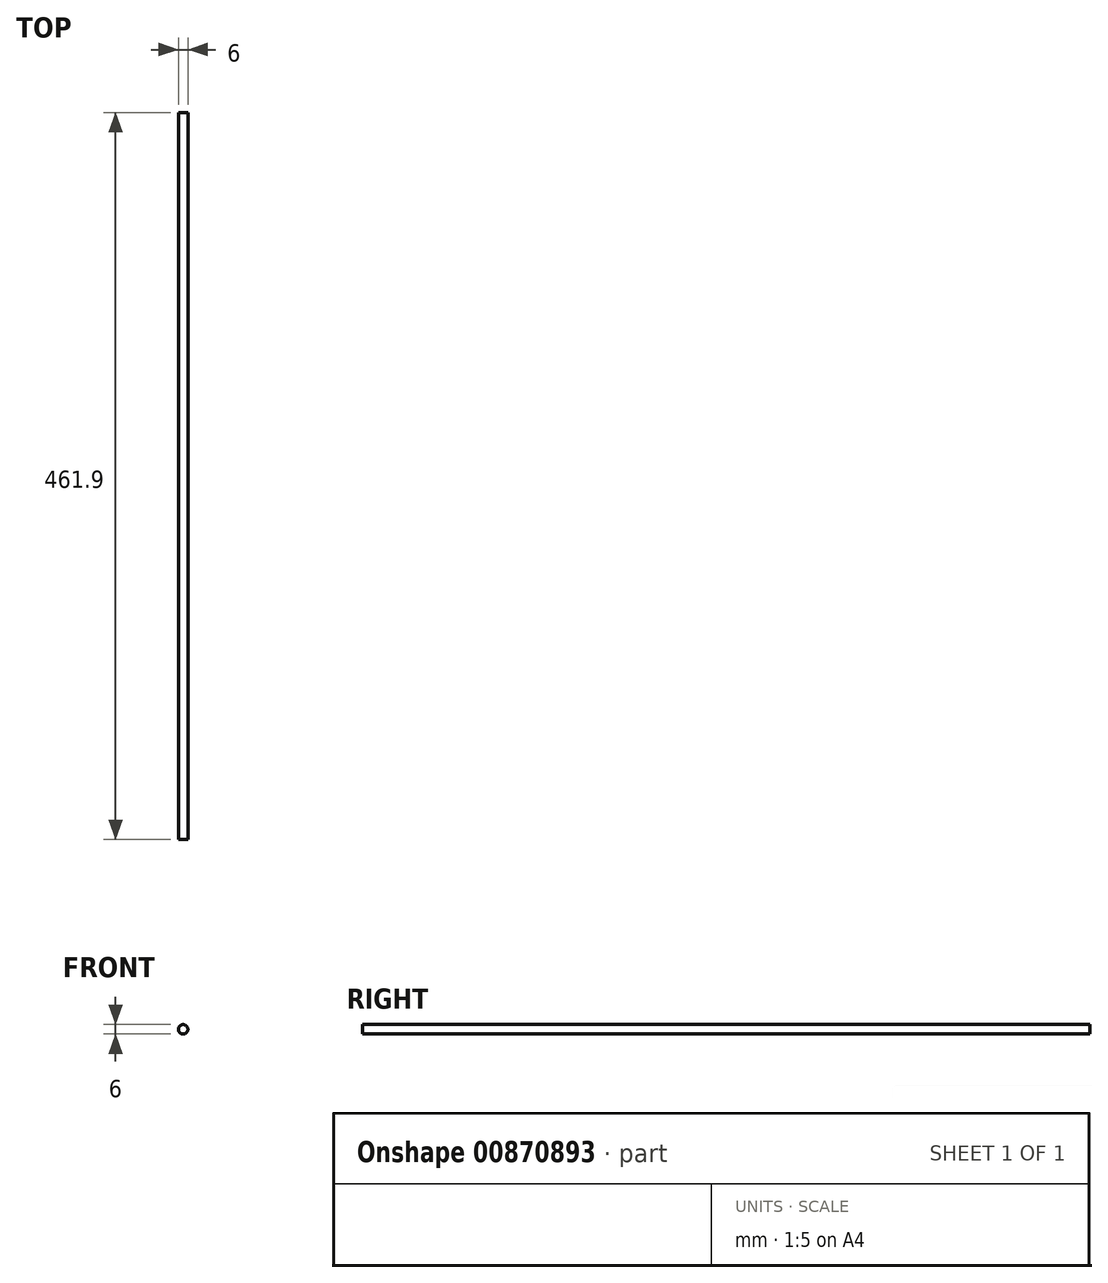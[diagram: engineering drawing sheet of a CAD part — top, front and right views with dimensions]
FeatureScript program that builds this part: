
annotation { "Feature Type Name" : "Feature", "Feature Type Description" : "" }
export const myFeature = defineFeature(function(context is Context, id is Id, definition is map)
    precondition{}
    {
        {
            var Q0;
            Q0=qCreatedBy(makeId("Front.planeOp"),FACE);
            var sketch = newSketch(context, id + "F0", { "sketchPlane" : qUnion([Q0])});
            skCircle(sketch, "E0", {"center": v(0, 0) * mm, "radius": 3 * mm});
            skSolve(sketch);
        }
        {
            var Q0;
            Q0=makeQuery(id+"F0.imprint","IMPRINT",FACE,{"disambiguationData":[TD([[makeQuery(id+"F0.imprint","IMPRINT",EDGE,{"derivedFrom":sQuery(id+"F0.wireOp",EDGE,"E0")}),1.0]])]});
            extrude(context, id + "F1", {"entities" : qUnion([Q0]), "depth" : (500 - (2 * 19.05)) * mm, "offsetDistance" : 25 * mm});
        }
    });
